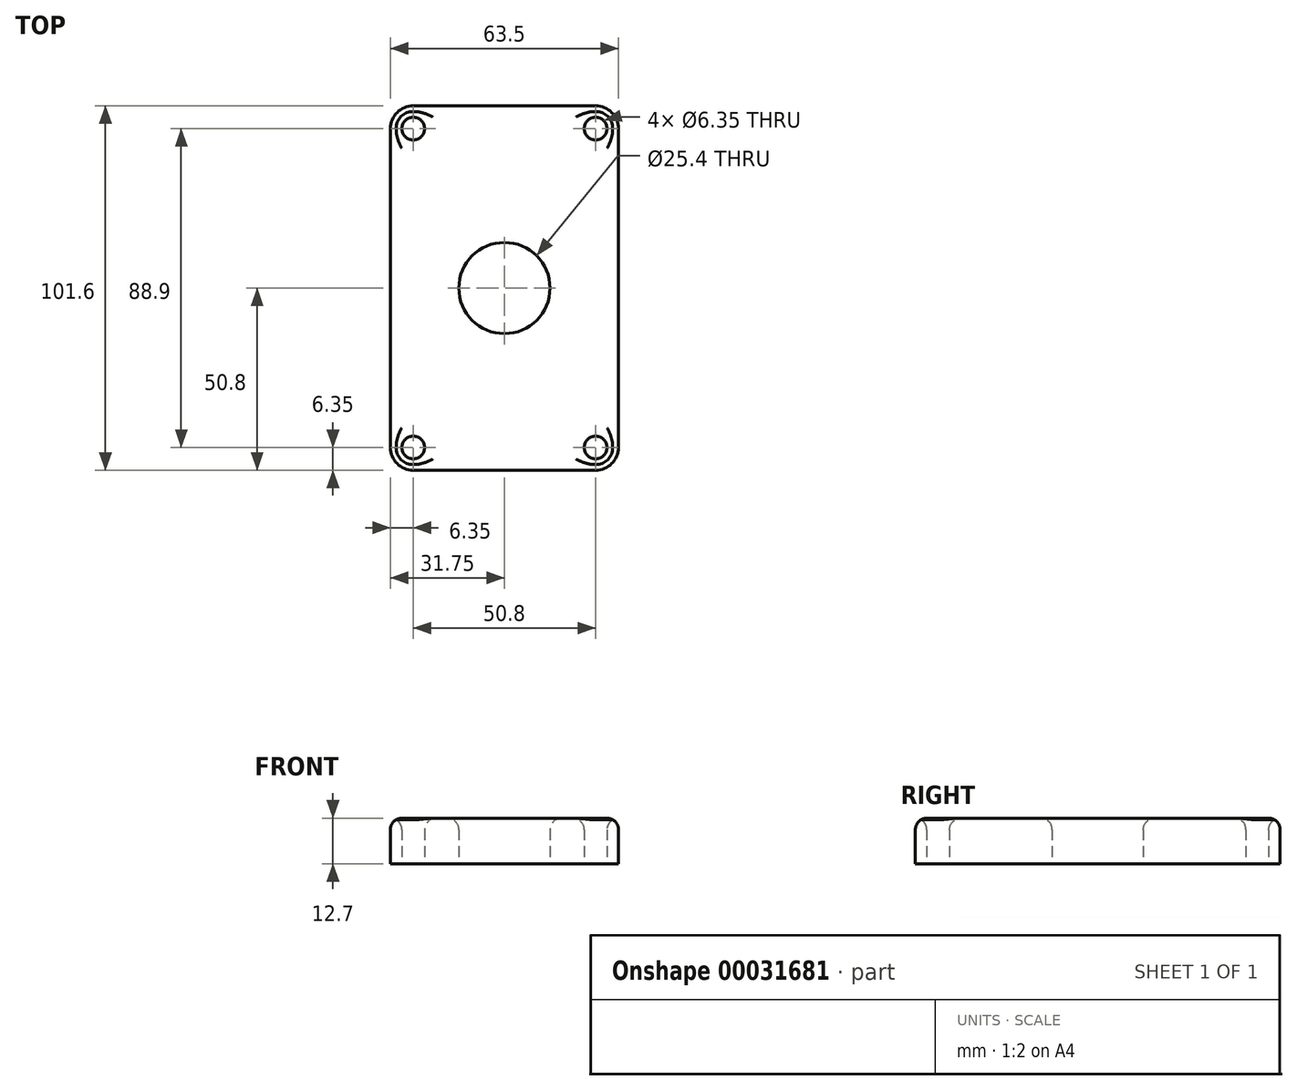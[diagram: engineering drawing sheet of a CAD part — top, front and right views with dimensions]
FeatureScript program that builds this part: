
annotation { "Feature Type Name" : "Feature", "Feature Type Description" : "" }
export const myFeature = defineFeature(function(context is Context, id is Id, definition is map)
    precondition{}
    {
        {
            var Q0;
            Q0=qCreatedBy(makeId("Top.planeOp"),FACE);
            var sketch = newSketch(context, id + "F0", { "sketchPlane" : qUnion([Q0])});
            skLineSegment(sketch, "E0.rect.bottom", {"start": v(25.4, 50.8) * mm, "end": v(-25.4, 50.8) * mm});
            skLineSegment(sketch, "E0.rect.top", {"start": v(25.4, -50.8) * mm, "end": v(-25.4, -50.8) * mm});
            skLineSegment(sketch, "E0.rect.left", {"start": v(31.75, 44.45) * mm, "end": v(31.75, -44.45) * mm});
            skLineSegment(sketch, "E0.rect.right", {"start": v(-31.75, 44.45) * mm, "end": v(-31.75, -44.45) * mm});
            skPoint(sketch, "E0.rect.middle", {"position": v(0, 0) * mm});
            skPoint(sketch, "E1.visualSharp", {"position": v(31.75, 50.8) * mm});
            skArc(sketch, "E1.filletArc", {"start": v(31.75, 44.45) * mm, "mid": v(29.9, 48.94) * mm, "end": v(25.4, 50.8) * mm});
            skPoint(sketch, "E2.visualSharp", {"position": v(-31.75, 50.8) * mm});
            skArc(sketch, "E2.filletArc", {"start": v(-25.4, 50.8) * mm, "mid": v(-29.9, 48.94) * mm, "end": v(-31.75, 44.45) * mm});
            skPoint(sketch, "E3.visualSharp", {"position": v(31.75, -50.8) * mm});
            skArc(sketch, "E3.filletArc", {"start": v(25.4, -50.8) * mm, "mid": v(29.9, -48.94) * mm, "end": v(31.75, -44.45) * mm});
            skPoint(sketch, "E4.visualSharp", {"position": v(-31.75, -50.8) * mm});
            skArc(sketch, "E4.filletArc", {"start": v(-31.75, -44.45) * mm, "mid": v(-29.9, -48.94) * mm, "end": v(-25.4, -50.8) * mm});
            skCircle(sketch, "E5", {"center": v(0, 0) * mm, "radius": 12.7 * mm});
            skCircle(sketch, "E6", {"center": v(-25.4, 44.45) * mm, "radius": 3.18 * mm});
            skCircle(sketch, "E7", {"center": v(25.4, 44.45) * mm, "radius": 3.18 * mm});
            skCircle(sketch, "E8", {"center": v(25.4, -44.45) * mm, "radius": 3.18 * mm});
            skCircle(sketch, "E9", {"center": v(-25.4, -44.45) * mm, "radius": 3.18 * mm});
            skSolve(sketch);
        }
        {
            var Q0;
            Q0 = qSketchRegion(id + "F0", true);
            extrude(context, id + "F1", {"entities" : qUnion([Q0]), "depth" : 12.7 * mm});
        }
        {
            var Q0;
            Q0=makeQuery(id+"F1.opExtrude","CAP_FACE",FACE,{"disambiguationData":[OSD([sQuery(id+"F0.wireOp",EDGE,"E0.rect.bottom"),sQuery(id+"F0.wireOp",EDGE,"E0.rect.top"),sQuery(id+"F0.wireOp",EDGE,"E0.rect.left"),sQuery(id+"F0.wireOp",EDGE,"E0.rect.right"),sQuery(id+"F0.wireOp",EDGE,"E1.filletArc"),sQuery(id+"F0.wireOp",EDGE,"E2.filletArc"),sQuery(id+"F0.wireOp",EDGE,"E3.filletArc"),sQuery(id+"F0.wireOp",EDGE,"E4.filletArc"),sQuery(id+"F0.wireOp",EDGE,"E5"),sQuery(id+"F0.wireOp",EDGE,"E6"),sQuery(id+"F0.wireOp",EDGE,"E7"),sQuery(id+"F0.wireOp",EDGE,"E8"),sQuery(id+"F0.wireOp",EDGE,"E9")])],"isStart":false});
            fillet(context, id + "F2", {"entities" : qUnion([Q0]), "radius" : 3.17 * mm, "tangentPropagation" : true, "allowEdgeOverflow" : false});
        }
    });
